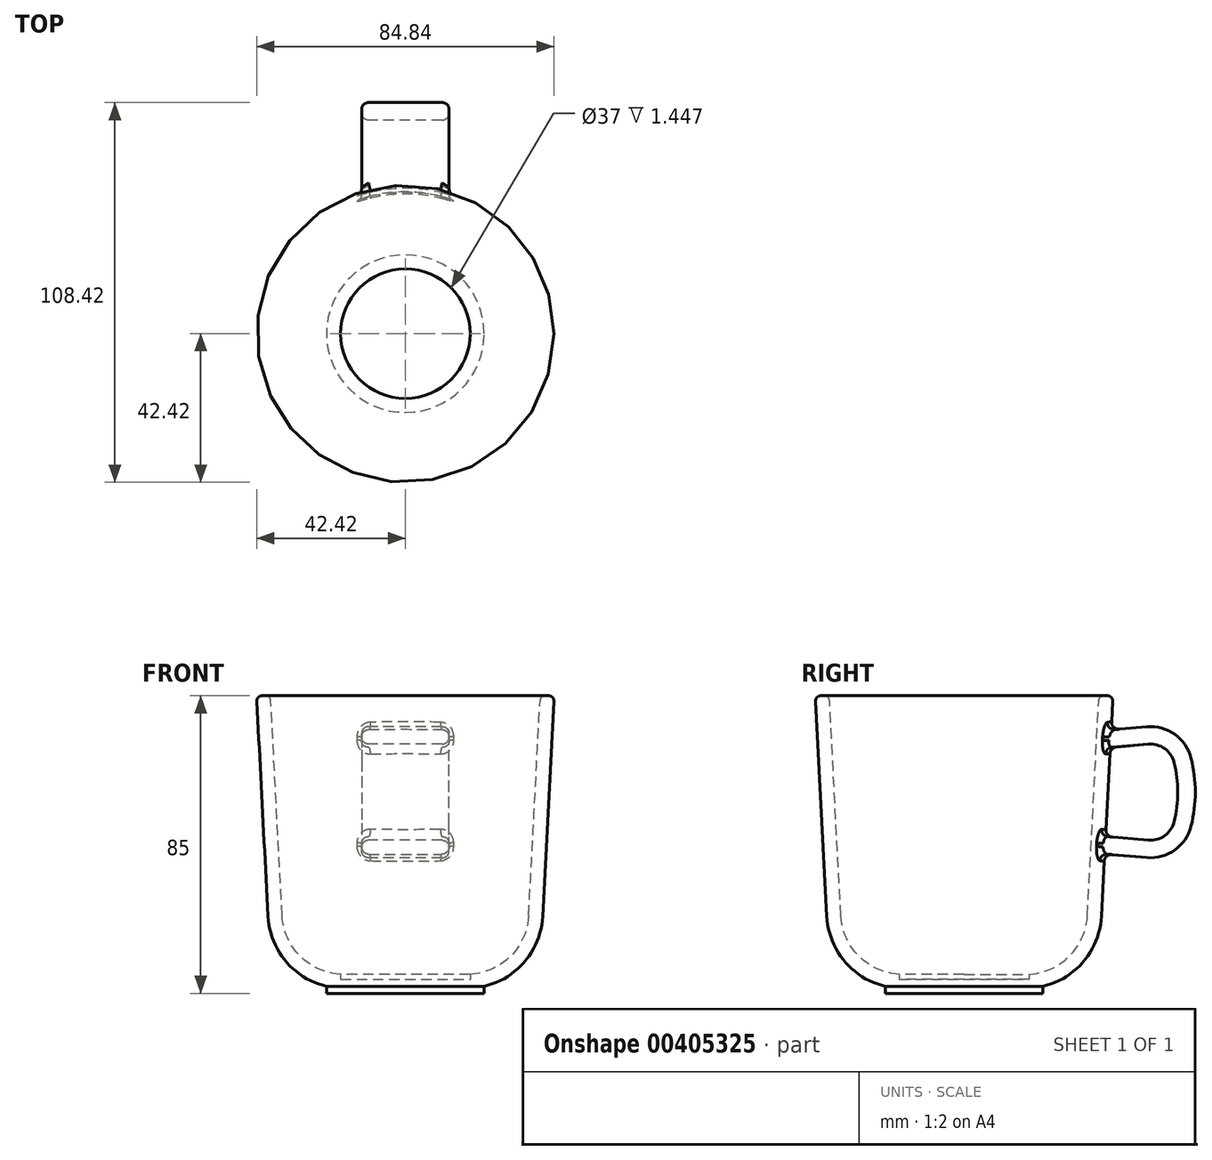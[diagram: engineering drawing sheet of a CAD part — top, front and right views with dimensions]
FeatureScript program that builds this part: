
annotation { "Feature Type Name" : "Feature", "Feature Type Description" : "" }
export const myFeature = defineFeature(function(context is Context, id is Id, definition is map)
    precondition{}
    {
        {
            var Q0;
            Q0=qCreatedBy(makeId("Front.planeOp"),FACE);
            var sketch = newSketch(context, id + "F0", { "sketchPlane" : qUnion([Q0])});
            skLineSegment(sketch, "E0", {"start": v(0, -23.82) * mm, "end": v(0, 0) * mm, "construction": true});
            skLineSegment(sketch, "E1", {"start": v(0, 0) * mm, "end": v(-22.5, 0) * mm});
            skLineSegment(sketch, "E2", {"start": v(-22.5, 0) * mm, "end": v(-22.5, 2) * mm});
            skArc(sketch, "E3", {"start": v(-39.2, 22) * mm, "mid": v(-34.18, 9.22) * mm, "end": v(-22.5, 2) * mm});
            skLineSegment(sketch, "E4", {"start": v(-39.2, 22) * mm, "end": v(-42.5, 85) * mm});
            skLineSegment(sketch, "E5", {"start": v(-42.5, 85) * mm, "end": v(0, 85) * mm});
            skLineSegment(sketch, "E6", {"start": v(0, 85) * mm, "end": v(0, 0) * mm});
            skSolve(sketch);
        }
        {
            var Q0;
            Q0=makeQuery(id+"F0.imprint","IMPRINT",FACE,{"disambiguationData":[TD([[makeQuery(id+"F0.imprint","IMPRINT",EDGE,{"derivedFrom":sQuery(id+"F0.wireOp",EDGE,"E1")}),-1.0]])]});
            var Q1;
            Q1=sQuery(id+"F0.wireOp",EDGE,"E0");
            revolve(context, id + "F1", {"entities" : qUnion([Q0]), "axis" : qUnion([Q1]), "revolveType" : RevolveType.FULL});
        }
        {
            var Q0;
            Q0=makeQuery(id+"F1.opRevolve","SWEPT_FACE",FACE,{"disambiguationData":[OSD([sQuery(id+"F0.wireOp",EDGE,"E5")])]});
            shell(context, id + "F2", {"entities" : qUnion([Q0]), "thickness" : 4 * mm});
        }
        {
            var Q0;
            Q0=qCreatedBy(makeId("Right.planeOp"),FACE);
            var sketch = newSketch(context, id + "F3", { "sketchPlane" : qUnion([Q0])});
            skLineSegment(sketch, "E7", {"start": v(39, 75) * mm, "end": v(52.13, 76.15) * mm});
            skArc(sketch, "E8", {"start": v(64.82, 67.08) * mm, "mid": v(60.15, 73.96) * mm, "end": v(52.13, 76.15) * mm});
            skArc(sketch, "E9", {"start": v(64.82, 47.83) * mm, "mid": v(66, 57.46) * mm, "end": v(64.82, 67.08) * mm});
            skArc(sketch, "E10", {"start": v(52.13, 38.76) * mm, "mid": v(60.15, 40.95) * mm, "end": v(64.82, 47.83) * mm});
            skLineSegment(sketch, "E11", {"start": v(52.13, 38.76) * mm, "end": v(38, 40) * mm});
            skLineSegment(sketch, "E12", {"start": v(39, 75) * mm, "end": v(96.97, 75) * mm, "construction": true});
            skPoint(sketch, "E13", {"position": v(66, 57.46) * mm});
            skSolve(sketch);
        }
        {
            var Q0;
            Q0=sQuery(id+"F3.wireOp",VERTEX,"E12.start");
            var Q1;
            Q1=sQuery(id+"F3.wireOp",EDGE,"E7");
            cPlane(context, id + "F4", {"entities" : qUnion([Q0, Q1]), "cplaneType" : CPlaneType.LINE_POINT, "offset" : 25 * mm, "width" : 150 * mm, "height" : 150 * mm});
        }
        {
            var Q0;
            Q0=qCreatedBy(id+"F4.planeOp",FACE);
            var sketch = newSketch(context, id + "F5", { "sketchPlane" : qUnion([Q0])});
            skLineSegment(sketch, "E14.bottom", {"start": v(12.5, 66.32) * mm, "end": v(-12.5, 66.32) * mm});
            skLineSegment(sketch, "E14.top", {"start": v(12.5, 71.32) * mm, "end": v(-12.5, 71.32) * mm});
            skLineSegment(sketch, "E14.left", {"start": v(12.5, 66.32) * mm, "end": v(12.5, 71.32) * mm});
            skLineSegment(sketch, "E14.right", {"start": v(-12.5, 66.32) * mm, "end": v(-12.5, 71.32) * mm});
            skPoint(sketch, "E14.middle", {"position": v(0, 68.82) * mm});
            skSolve(sketch);
        }
        {
            var Q0;
            Q0=makeQuery(id+"F1.opRevolve","SWEPT_FACE",FACE,{"disambiguationData":[OSD([sQuery(id+"F0.wireOp",EDGE,"E5")])]});
            fillet(context, id + "F6", {"entities" : qUnion([Q0]), "radius" : 1.5 * mm, "tangentPropagation" : true, "allowEdgeOverflow" : false});
        }
        {
            var Q0;
            Q0=makeQuery(id+"F5.imprint","IMPRINT",FACE,{"disambiguationData":[TD([[makeQuery(id+"F5.imprint","IMPRINT",EDGE,{"derivedFrom":sQuery(id+"F5.wireOp",EDGE,"E14.bottom")}),-1.0]])]});
            var Q1;
            Q1=sQuery(id+"F5.wireOp",EDGE,"E14.top");
            var Q2;
            Q2=sQuery(id+"F5.wireOp",EDGE,"E14.left");
            var Q3;
            Q3=sQuery(id+"F5.wireOp",EDGE,"E14.bottom");
            var Q4;
            Q4=sQuery(id+"F5.wireOp",EDGE,"E14.right");
            var Q5;
            Q5=sQuery(id+"F3.wireOp",EDGE,"E7");
            var Q6;
            Q6=sQuery(id+"F3.wireOp",EDGE,"E8");
            var Q7;
            Q7=sQuery(id+"F3.wireOp",EDGE,"E9");
            var Q8;
            Q8=sQuery(id+"F3.wireOp",EDGE,"E10");
            var Q9;
            Q9=sQuery(id+"F3.wireOp",EDGE,"E11");
            sweep(context, id + "F7", {"operationType" : NewBodyOperationType.ADD, "profiles" : qUnion([Q0]), "surfaceProfiles" : qUnion([Q1, Q2, Q3, Q4]), "path" : qUnion([Q5, Q6, Q7, Q8, Q9])});
        }
        {
            var Q0;
            Q0=makeQuery(id+"F7.opSweep","SWEPT_EDGE",EDGE,{"disambiguationData":[OSD([sQuery(id+"F3.wireOp",EDGE,"E9"),sQuery(id+"F5.wireOp",VERTEX,"E14.right.end")])]});
            var Q1;
            Q1=makeQuery(id+"F7.opSweep","SWEPT_EDGE",EDGE,{"disambiguationData":[OSD([sQuery(id+"F3.wireOp",EDGE,"E9"),sQuery(id+"F5.wireOp",VERTEX,"E14.left.end")])]});
            fillet(context, id + "F8", {"entities" : qUnion([Q0, Q1]), "radius" : 2 * mm, "tangentPropagation" : true, "allowEdgeOverflow" : false});
        }
        {
            var Q0;
            Q0=makeQuery(id+"F7.boolean.opBoolean","INTERSECT",EDGE,{"derivedFrom":[makeQuery(id+"F1.opRevolve","SWEPT_FACE",FACE,{"disambiguationData":[OSD([sQuery(id+"F0.wireOp",EDGE,"E4")])]}),makeQuery(id+"F7.opSweep","SWEPT_FACE",FACE,{"disambiguationData":[OSD([sQuery(id+"F3.wireOp",EDGE,"E7"),sQuery(id+"F5.wireOp",EDGE,"E14.top")])]})]});
            var Q1;
            Q1=makeQuery(id+"F7.boolean.opBoolean","INTERSECT",EDGE,{"derivedFrom":[makeQuery(id+"F1.opRevolve","SWEPT_FACE",FACE,{"disambiguationData":[OSD([sQuery(id+"F0.wireOp",EDGE,"E4")])]}),makeQuery(id+"F7.opSweep","SWEPT_FACE",FACE,{"disambiguationData":[OSD([sQuery(id+"F3.wireOp",EDGE,"E11"),sQuery(id+"F5.wireOp",EDGE,"E14.bottom")])]})]});
            fillet(context, id + "F9", {"entities" : qUnion([Q0, Q1]), "radius" : 2 * mm, "tangentPropagation" : true, "allowEdgeOverflow" : false});
        }
    });
